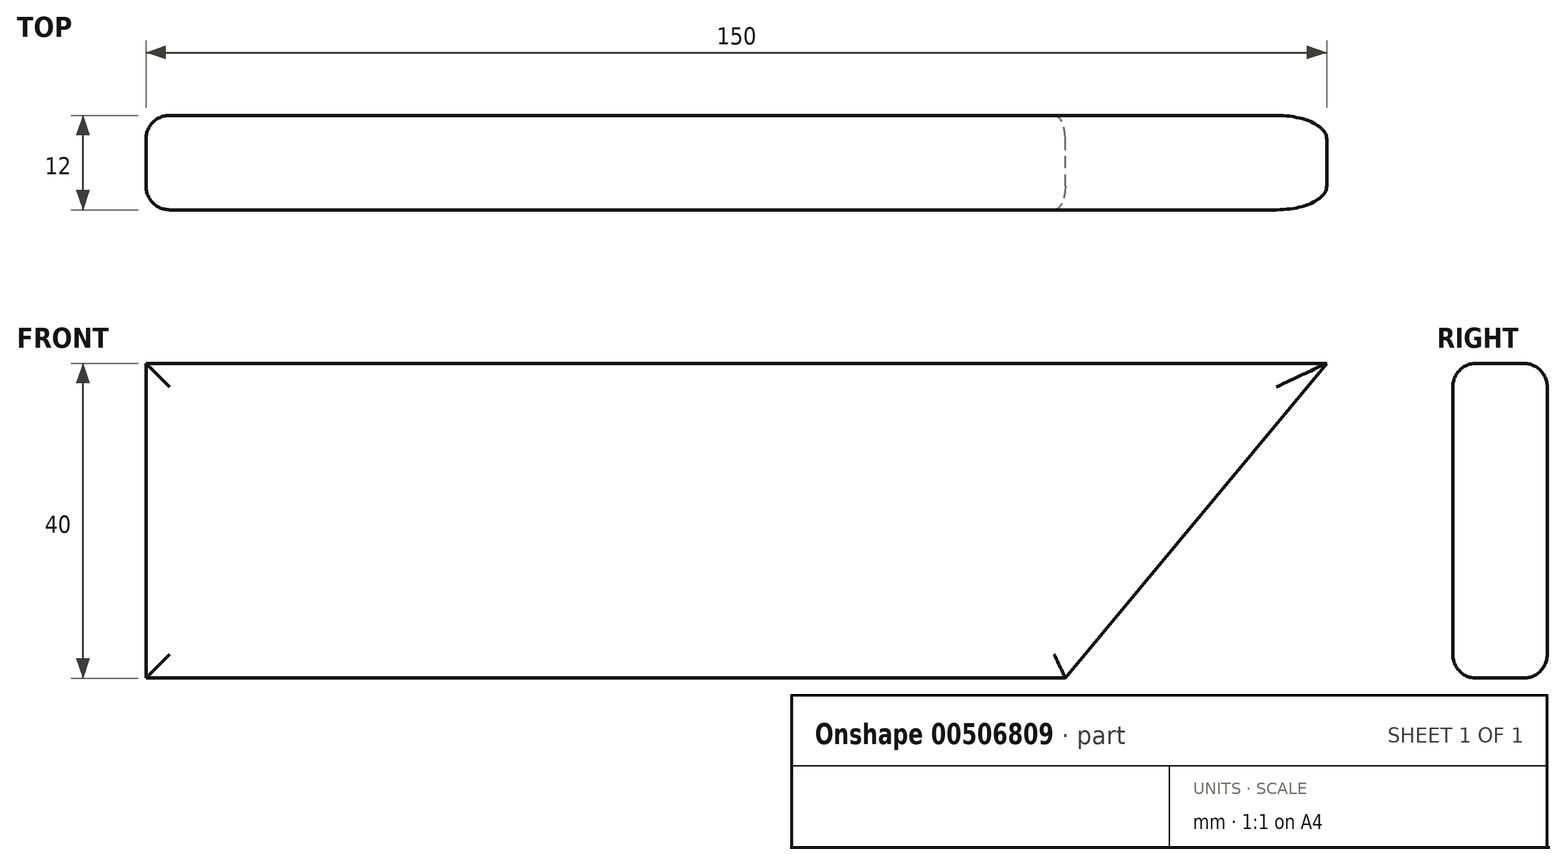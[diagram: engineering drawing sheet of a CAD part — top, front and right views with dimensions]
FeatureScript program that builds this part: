
annotation { "Feature Type Name" : "Feature", "Feature Type Description" : "" }
export const myFeature = defineFeature(function(context is Context, id is Id, definition is map)
    precondition{}
    {
        {
            var Q0;
            Q0=qCreatedBy(makeId("Front.planeOp"),FACE);
            var sketch = newSketch(context, id + "F0", { "sketchPlane" : qUnion([Q0])});
            skLineSegment(sketch, "E0.bottom", {"start": v(-629.35, -2.53) * mm, "end": v(-479.35, -2.53) * mm});
            skLineSegment(sketch, "E0.top", {"start": v(-629.35, -42.53) * mm, "end": v(-479.35, -42.53) * mm});
            skLineSegment(sketch, "E0.left", {"start": v(-629.35, -2.53) * mm, "end": v(-629.35, -42.53) * mm});
            skLineSegment(sketch, "E0.right", {"start": v(-479.35, -2.53) * mm, "end": v(-479.35, -42.53) * mm});
            skLineSegment(sketch, "E1", {"start": v(-479.35, -2.53) * mm, "end": v(-512.57, -42.53) * mm});
            skSolve(sketch);
        }
        {
            var Q0;
            Q0=makeQuery(id+"F0.imprint","IMPRINT",FACE,{"disambiguationData":[TD([[makeQuery(id+"F0.imprint","IMPRINT",EDGE,{"derivedFrom":sQuery(id+"F0.wireOp",EDGE,"E0.bottom")}),-1.0]])]});
            extrude(context, id + "F1", {"entities" : qUnion([Q0]), "depth" : 12 * mm});
        }
        {
            var Q0;
            Q0=makeQuery(id+"F1.opExtrude","SWEPT_FACE",FACE,{"disambiguationData":[OSD([sQuery(id+"F0.wireOp",EDGE,"E0.left")])]});
            var sketch = newSketch(context, id + "F2", { "sketchPlane" : qUnion([Q0])});
            skLineSegment(sketch, "E2", {"start": v(6, -2.53) * mm, "end": v(6, -42.53) * mm});
            skSolve(sketch);
        }
        {
            var Q0;
            Q0=makeQuery(id+"F1.opExtrude","CAP_FACE",FACE,{"disambiguationData":[OSD([sQuery(id+"F0.wireOp",EDGE,"E0.bottom"),sQuery(id+"F0.wireOp",EDGE,"E0.top"),sQuery(id+"F0.wireOp",EDGE,"E0.left"),sQuery(id+"F0.wireOp",EDGE,"E0.right")])],"isStart":false});
            var Q1;
            Q1=makeQuery(id+"F1.opExtrude","CAP_FACE",FACE,{"disambiguationData":[OSD([sQuery(id+"F0.wireOp",EDGE,"E0.bottom"),sQuery(id+"F0.wireOp",EDGE,"E0.top"),sQuery(id+"F0.wireOp",EDGE,"E0.left"),sQuery(id+"F0.wireOp",EDGE,"E0.right")])],"isStart":true});
            fillet(context, id + "F3", {"entities" : qUnion([Q0, Q1]), "radius" : 3 * mm, "tangentPropagation" : true, "allowEdgeOverflow" : false});
        }
    });
